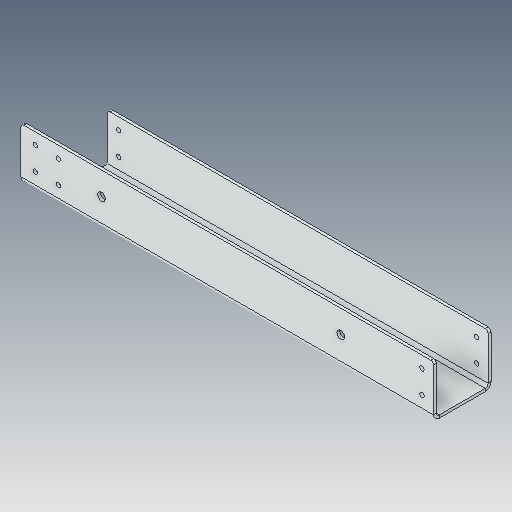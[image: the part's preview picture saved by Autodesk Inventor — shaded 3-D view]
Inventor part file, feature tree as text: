
AUTODESK INVENTOR PART (.ipt)
format: ipt  version: 2023.5 (Build 275446000, 446)  size: 139,264 bytes
history: native  units: in
note: dims shown in document units (in); Inventor stores cm internally (conversion verified against a paired STEP export)
features: fillet x1
ambient origin geometry x8: Origin, YZ Plane, XZ Plane, XY Plane, X Axis, Y Axis, Z Axis, Center Point
bodies: Solid1 (feature_tree)
feature tree (1):
  fillet  "Fillet1"  [1 undecoded]
note: 1 required parameter value undecoded (feature->parameter linkage not recoverable at this tier; creation-order binding heuristic only, values carry confidence <= 0.55)
